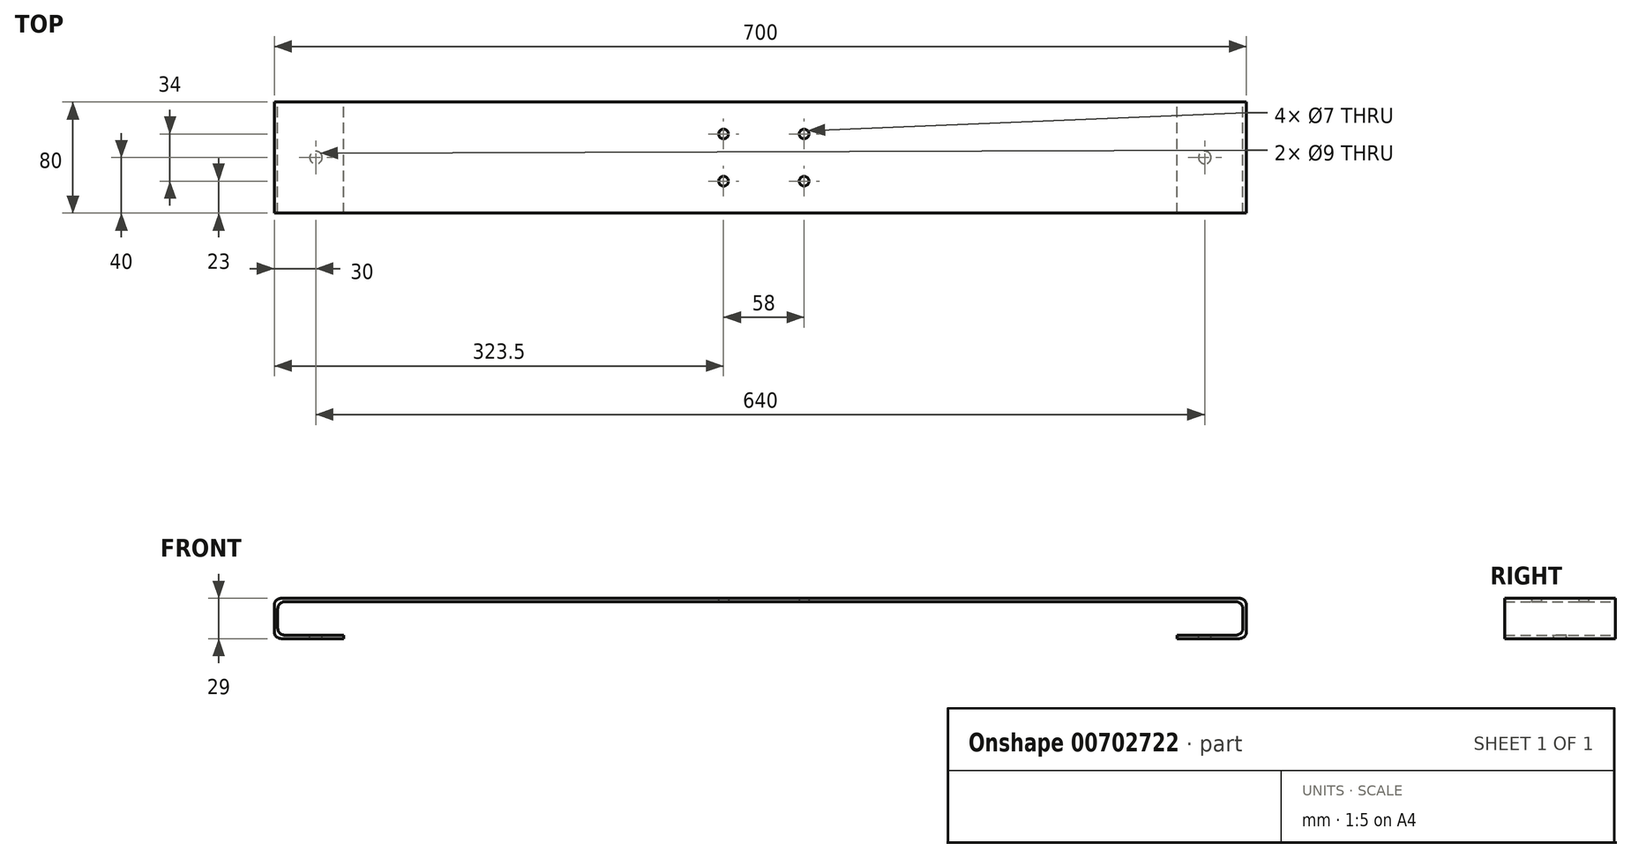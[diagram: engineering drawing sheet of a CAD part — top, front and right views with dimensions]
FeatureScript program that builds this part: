
annotation { "Feature Type Name" : "Feature", "Feature Type Description" : "" }
export const myFeature = defineFeature(function(context is Context, id is Id, definition is map)
    precondition{}
    {
        {
            var Q0;
            Q0=qCreatedBy(makeId("Front.planeOp"),FACE);
            var sketch = newSketch(context, id + "F0", { "sketchPlane" : qUnion([Q0])});
            skLineSegment(sketch, "E0", {"start": v(0, 0) * mm, "end": v(50, 0) * mm});
            skLineSegment(sketch, "E1", {"start": v(0, 0) * mm, "end": v(0, 29) * mm});
            skLineSegment(sketch, "E2", {"start": v(0, 29) * mm, "end": v(700, 29) * mm});
            skLineSegment(sketch, "E3", {"start": v(700, 29) * mm, "end": v(700, 0) * mm});
            skLineSegment(sketch, "E4", {"start": v(700, 0) * mm, "end": v(650, 0) * mm});
            skLineSegment(sketch, "E5.0", {"start": v(2.5, 2.5) * mm, "end": v(50, 2.5) * mm});
            skLineSegment(sketch, "E5.1", {"start": v(697.5, 2.5) * mm, "end": v(650, 2.5) * mm});
            skLineSegment(sketch, "E5.2", {"start": v(697.5, 26.5) * mm, "end": v(697.5, 2.5) * mm});
            skLineSegment(sketch, "E5.3", {"start": v(2.5, 26.5) * mm, "end": v(697.5, 26.5) * mm});
            skLineSegment(sketch, "E5.4", {"start": v(2.5, 2.5) * mm, "end": v(2.5, 26.5) * mm});
            skLineSegment(sketch, "E6", {"start": v(50, 2.5) * mm, "end": v(50, 0) * mm});
            skLineSegment(sketch, "E7", {"start": v(650, 2.5) * mm, "end": v(650, 0) * mm});
            skSolve(sketch);
        }
        {
            var Q0;
            Q0=qSketchRegion(id+"F0",true);
            extrude(context, id + "F1", {"entities" : qUnion([Q0]), "endBound" : BoundingType.SYMMETRIC, "depth" : 80 * mm, "offsetDistance" : 25 * mm});
        }
        {
            var Q0;
            Q0=makeQuery(id+"F1.opExtrude","SWEPT_FACE",FACE,{"disambiguationData":[OSD([sQuery(id+"F0.wireOp",EDGE,"E5.0")])]});
            var sketch = newSketch(context, id + "F2", { "sketchPlane" : qUnion([Q0])});
            skLineSegment(sketch, "E8", {"start": v(50, 0) * mm, "end": v(30, 0) * mm});
            skSolve(sketch);
        }
        {
            var Q0;
            Q0=makeQuery(id+"F1.opExtrude","SWEPT_FACE",FACE,{"disambiguationData":[OSD([sQuery(id+"F0.wireOp",EDGE,"E5.1")])]});
            var sketch = newSketch(context, id + "F3", { "sketchPlane" : qUnion([Q0])});
            skLineSegment(sketch, "E9", {"start": v(650, 0) * mm, "end": v(670, 0) * mm});
            skSolve(sketch);
        }
        {
            var Q0;
            Q0=sQuery(id+"F3.wireOp",VERTEX,"E9.end");
            var Q1;
            Q1=makeQuery(id+"F1.opExtrude","SWEPT_BODY",BODY,{"disambiguationData":[OSD([sQuery(id+"F0.wireOp",EDGE,"E0"),sQuery(id+"F0.wireOp",EDGE,"E1"),sQuery(id+"F0.wireOp",EDGE,"E2"),sQuery(id+"F0.wireOp",EDGE,"E3"),sQuery(id+"F0.wireOp",EDGE,"E4"),sQuery(id+"F0.wireOp",EDGE,"E5.0"),sQuery(id+"F0.wireOp",EDGE,"E5.1"),sQuery(id+"F0.wireOp",EDGE,"E5.2"),sQuery(id+"F0.wireOp",EDGE,"E5.3"),sQuery(id+"F0.wireOp",EDGE,"E5.4"),sQuery(id+"F0.wireOp",EDGE,"E6"),sQuery(id+"F0.wireOp",EDGE,"E7")])]});
            hole(context, id + "F4", {"style" : HoleStyle.SIMPLE, "endStyle" : HoleEndStyle.BLIND, "holeDiameter" : 9 * mm, "majorDiameter" : 5 * mm, "holeDepth" : 12 * mm, "isTappedThrough" : true, "tappedDepth" : 12 * mm, "tapClearance" : 3, "locations" : qUnion([Q0]), "scope" : qUnion([Q1])});
        }
        {
            var Q0;
            Q0=sQuery(id+"F2.wireOp",VERTEX,"E8.end");
            var Q1;
            Q1=makeQuery(id+"F1.opExtrude","SWEPT_BODY",BODY,{"disambiguationData":[OSD([sQuery(id+"F0.wireOp",EDGE,"E0"),sQuery(id+"F0.wireOp",EDGE,"E1"),sQuery(id+"F0.wireOp",EDGE,"E2"),sQuery(id+"F0.wireOp",EDGE,"E3"),sQuery(id+"F0.wireOp",EDGE,"E4"),sQuery(id+"F0.wireOp",EDGE,"E5.0"),sQuery(id+"F0.wireOp",EDGE,"E5.1"),sQuery(id+"F0.wireOp",EDGE,"E5.2"),sQuery(id+"F0.wireOp",EDGE,"E5.3"),sQuery(id+"F0.wireOp",EDGE,"E5.4"),sQuery(id+"F0.wireOp",EDGE,"E6"),sQuery(id+"F0.wireOp",EDGE,"E7")])]});
            hole(context, id + "F5", {"style" : HoleStyle.SIMPLE, "endStyle" : HoleEndStyle.BLIND, "holeDiameter" : 9 * mm, "majorDiameter" : 5 * mm, "holeDepth" : 12 * mm, "isTappedThrough" : true, "tappedDepth" : 12 * mm, "tapClearance" : 3, "locations" : qUnion([Q0]), "scope" : qUnion([Q1])});
        }
        {
            var Q0;
            Q0=makeQuery(id+"F1.opExtrude","SWEPT_FACE",FACE,{"disambiguationData":[OSD([sQuery(id+"F0.wireOp",EDGE,"E5.3")])]});
            var sketch = newSketch(context, id + "F6", { "sketchPlane" : qUnion([Q0])});
            skPoint(sketch, "E10.middle", {"position": v(247.5, 0) * mm});
            skLineSegment(sketch, "E11.bottom", {"start": v(381.5, -17) * mm, "end": v(323.5, -17) * mm});
            skLineSegment(sketch, "E11.top", {"start": v(381.5, 17) * mm, "end": v(323.5, 17) * mm});
            skLineSegment(sketch, "E11.left", {"start": v(381.5, -17) * mm, "end": v(381.5, 17) * mm});
            skLineSegment(sketch, "E11.right", {"start": v(323.5, -17) * mm, "end": v(323.5, 17) * mm});
            skPoint(sketch, "E11.middle", {"position": v(352.5, 0) * mm});
            skLineSegment(sketch, "E12", {"start": v(2.5, 0) * mm, "end": v(352.5, 0) * mm});
            skSolve(sketch);
        }
        {
            var Q0;
            Q0=sQuery(id+"F6.wireOp",VERTEX,"E10.left.start");
            var Q1;
            Q1=sQuery(id+"F6.wireOp",VERTEX,"E10.right.start");
            var Q2;
            Q2=sQuery(id+"F6.wireOp",VERTEX,"E10.right.end");
            var Q3;
            Q3=sQuery(id+"F6.wireOp",VERTEX,"E10.left.end");
            var Q4;
            Q4=sQuery(id+"F6.wireOp",VERTEX,"E11.bottom.start");
            var Q5;
            Q5=sQuery(id+"F6.wireOp",VERTEX,"E11.right.start");
            var Q6;
            Q6=sQuery(id+"F6.wireOp",VERTEX,"E11.right.end");
            var Q7;
            Q7=sQuery(id+"F6.wireOp",VERTEX,"E11.left.end");
            var Q8;
            Q8=makeQuery(id+"F1.opExtrude","SWEPT_BODY",BODY,{"disambiguationData":[OSD([sQuery(id+"F0.wireOp",EDGE,"E0"),sQuery(id+"F0.wireOp",EDGE,"E1"),sQuery(id+"F0.wireOp",EDGE,"E2"),sQuery(id+"F0.wireOp",EDGE,"E3"),sQuery(id+"F0.wireOp",EDGE,"E4"),sQuery(id+"F0.wireOp",EDGE,"E5.0"),sQuery(id+"F0.wireOp",EDGE,"E5.1"),sQuery(id+"F0.wireOp",EDGE,"E5.2"),sQuery(id+"F0.wireOp",EDGE,"E5.3"),sQuery(id+"F0.wireOp",EDGE,"E5.4"),sQuery(id+"F0.wireOp",EDGE,"E6"),sQuery(id+"F0.wireOp",EDGE,"E7")])]});
            hole(context, id + "F7", {"style" : HoleStyle.SIMPLE, "endStyle" : HoleEndStyle.THROUGH, "holeDiameter" : 7 * mm, "majorDiameter" : 5 * mm, "isTappedThrough" : true, "tappedDepth" : 12 * mm, "tapClearance" : 3, "locations" : qUnion([Q0, Q1, Q2, Q3, Q4, Q5, Q6, Q7]), "scope" : qUnion([Q8])});
        }
        {
            var Q0;
            Q0=makeQuery(id+"F1.opExtrude","SWEPT_EDGE",EDGE,{"disambiguationData":[OSD([sQuery(id+"F0.wireOp",EDGE,"E1"),sQuery(id+"F0.wireOp",EDGE,"E2")])]});
            var Q1;
            Q1=makeQuery(id+"F1.opExtrude","SWEPT_EDGE",EDGE,{"disambiguationData":[OSD([sQuery(id+"F0.wireOp",EDGE,"E0"),sQuery(id+"F0.wireOp",EDGE,"E1")])]});
            var Q2;
            Q2=makeQuery(id+"F1.opExtrude","SWEPT_EDGE",EDGE,{"disambiguationData":[OSD([sQuery(id+"F0.wireOp",EDGE,"E2"),sQuery(id+"F0.wireOp",EDGE,"E3")])]});
            var Q3;
            Q3=makeQuery(id+"F1.opExtrude","SWEPT_EDGE",EDGE,{"disambiguationData":[OSD([sQuery(id+"F0.wireOp",EDGE,"E3"),sQuery(id+"F0.wireOp",EDGE,"E4")])]});
            var Q4;
            Q4=makeQuery(id+"F1.opExtrude","SWEPT_EDGE",EDGE,{"disambiguationData":[OSD([sQuery(id+"F0.wireOp",EDGE,"E5.0"),sQuery(id+"F0.wireOp",EDGE,"E5.4")])]});
            var Q5;
            Q5=makeQuery(id+"F1.opExtrude","SWEPT_EDGE",EDGE,{"disambiguationData":[OSD([sQuery(id+"F0.wireOp",EDGE,"E5.3"),sQuery(id+"F0.wireOp",EDGE,"E5.4")])]});
            var Q6;
            Q6=makeQuery(id+"F1.opExtrude","SWEPT_EDGE",EDGE,{"disambiguationData":[OSD([sQuery(id+"F0.wireOp",EDGE,"E5.1"),sQuery(id+"F0.wireOp",EDGE,"E5.2")])]});
            var Q7;
            Q7=makeQuery(id+"F1.opExtrude","SWEPT_EDGE",EDGE,{"disambiguationData":[OSD([sQuery(id+"F0.wireOp",EDGE,"E5.2"),sQuery(id+"F0.wireOp",EDGE,"E5.3")])]});
            fillet(context, id + "F8", {"entities" : qUnion([Q0, Q1, Q2, Q3, Q4, Q5, Q6, Q7]), "radius" : 5 * mm, "tangentPropagation" : true, "allowEdgeOverflow" : false});
        }
    });
